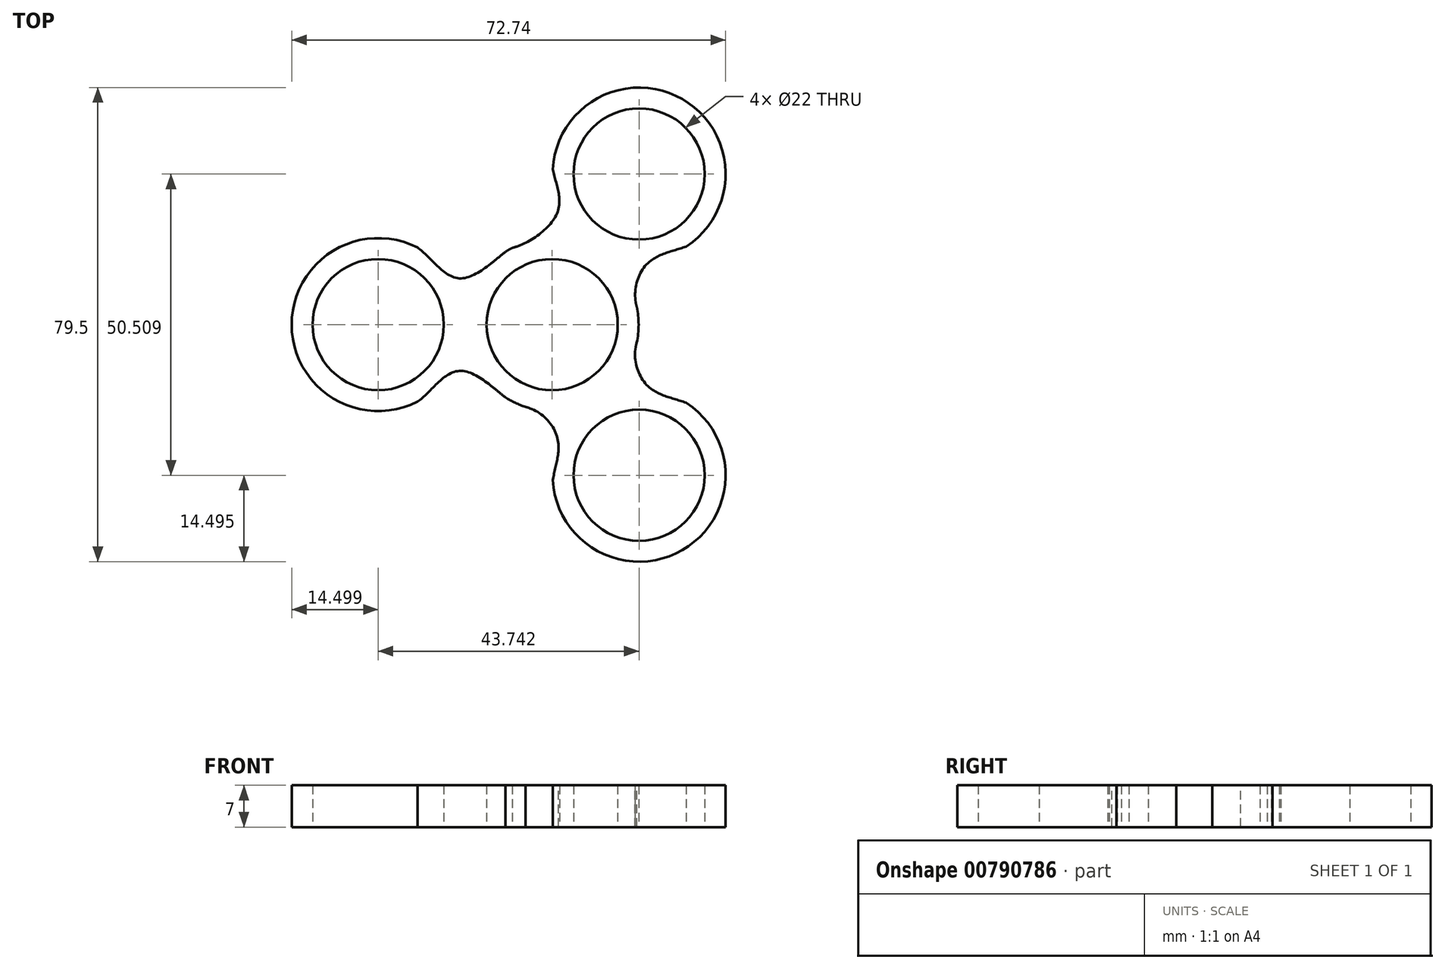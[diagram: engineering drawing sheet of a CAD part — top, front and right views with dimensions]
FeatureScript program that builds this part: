
annotation { "Feature Type Name" : "Feature", "Feature Type Description" : "" }
export const myFeature = defineFeature(function(context is Context, id is Id, definition is map)
    precondition{}
    {
        {
            var Q0;
            Q0=qCreatedBy(makeId("Top.planeOp"),FACE);
            var sketch = newSketch(context, id + "F0", { "sketchPlane" : qUnion([Q0])});
            skCircle(sketch, "E0", {"center": v(0, 0) * mm, "radius": 14.5 * mm});
            skCircle(sketch, "E1", {"center": v(-29.16, 0) * mm, "radius": 14.5 * mm});
            skCircle(sketch, "E2", {"center": v(14.58, 25.25) * mm, "radius": 14.5 * mm});
            skCircle(sketch, "E3", {"center": v(14.58, -25.25) * mm, "radius": 14.5 * mm});
            skLineSegment(sketch, "E4", {"start": v(14.58, 25.25) * mm, "end": v(-29.16, 0) * mm, "construction": true});
            skLineSegment(sketch, "E5", {"start": v(14.58, -25.25) * mm, "end": v(-29.16, 0) * mm, "construction": true});
            skLineSegment(sketch, "E6", {"start": v(14.58, -25.25) * mm, "end": v(14.58, 25.25) * mm, "construction": true});
            skLineSegment(sketch, "E7", {"start": v(14.58, 25.25) * mm, "end": v(0, 0) * mm, "construction": true});
            skLineSegment(sketch, "E8", {"start": v(-29.16, 0) * mm, "end": v(0, 0) * mm, "construction": true});
            skLineSegment(sketch, "E9", {"start": v(14.58, -25.25) * mm, "end": v(0, 0) * mm, "construction": true});
            skPoint(sketch, "E10.0.internal.snap0", {"position": v(-7.3, 12.63) * mm});
            skFitSpline(sketch, "E11", {"points": [v(-22.59, 12.92) * mm, v(-15.7, 7.77) * mm, v(-7.81, 12.22) * mm], "startDerivative": vector(12.46, -7.7) * mm, "endDerivative": vector(11.22, 8.55) * mm});
            skLineSegment(sketch, "E12", {"start": v(-29.16, 0) * mm, "end": v(-22.59, 12.92) * mm, "construction": true});
            skPoint(sketch, "E13", {"position": v(-22.59, -12.92) * mm});
            skLineSegment(sketch, "E14", {"start": v(-22.59, -12.92) * mm, "end": v(0, 0) * mm, "construction": true});
            skLineSegment(sketch, "E15", {"start": v(-22.59, 12.92) * mm, "end": v(0, 0) * mm, "construction": true});
            skPoint(sketch, "E16", {"position": v(-20.54, -11.66) * mm});
            skLineSegment(sketch, "E17", {"start": v(-20.54, -11.66) * mm, "end": v(0, 0) * mm, "construction": true});
            skLineSegment(sketch, "E18", {"start": v(-20.54, 11.66) * mm, "end": v(0, 0) * mm, "construction": true});
            skPoint(sketch, "E19", {"position": v(-9.7, -10.77) * mm});
            skLineSegment(sketch, "E20", {"start": v(-9.7, 10.77) * mm, "end": v(-29.16, 0) * mm, "construction": true});
            skLineSegment(sketch, "E21", {"start": v(-9.7, -10.77) * mm, "end": v(-29.16, 0) * mm, "construction": true});
            skPoint(sketch, "E22", {"position": v(-7.81, -12.22) * mm});
            skLineSegment(sketch, "E23", {"start": v(-7.81, -12.22) * mm, "end": v(-29.16, 0) * mm, "construction": true});
            skLineSegment(sketch, "E24", {"start": v(-7.81, 12.22) * mm, "end": v(-29.16, 0) * mm, "construction": true});
            skFitSpline(sketch, "E25.MirrorCS", {"points": [v(-22.59, -12.92) * mm, v(-15.7, -7.77) * mm, v(-7.81, -12.22) * mm], "startDerivative": vector(12.46, 7.7) * mm, "endDerivative": vector(11.22, -8.55) * mm});
            skPoint(sketch, "E26", {"position": v(22.49, 13.1) * mm});
            skLineSegment(sketch, "E27", {"start": v(22.49, 13.1) * mm, "end": v(0, 0) * mm, "construction": true});
            skLineSegment(sketch, "E28", {"start": v(14.49, 0.66) * mm, "end": v(14.58, 25.25) * mm, "construction": true});
            skFitSpline(sketch, "E29", {"points": [v(22.49, 13.1) * mm, v(15.9, 10.17) * mm, v(14.19, 2.99) * mm], "startDerivative": vector(-14.26, -4.9) * mm, "endDerivative": vector(4.41, -14.5) * mm});
            skPoint(sketch, "E30", {"position": v(0.1, 26.02) * mm});
            skLineSegment(sketch, "E31", {"start": v(0.1, 26.02) * mm, "end": v(0, 0) * mm, "construction": true});
            skPoint(sketch, "E32", {"position": v(-6.67, 12.87) * mm});
            skLineSegment(sketch, "E33", {"start": v(-6.67, 12.87) * mm, "end": v(14.58, 25.25) * mm, "construction": true});
            skFitSpline(sketch, "E34.MirrorCS", {"points": [v(0.1, 26.02) * mm, v(0.9, 18.84) * mm, v(-6.67, 12.87) * mm], "startDerivative": vector(2.98, -14.78) * mm, "endDerivative": vector(-14.74, -3.52) * mm});
            skPoint(sketch, "E35", {"position": v(14.49, -0.66) * mm});
            skPoint(sketch, "E36", {"position": v(22.49, -13.1) * mm});
            skPoint(sketch, "E37", {"position": v(0.1, -26.02) * mm});
            skPoint(sketch, "E38", {"position": v(-6.67, -12.87) * mm});
            skLineSegment(sketch, "E39", {"start": v(0.1, -26.02) * mm, "end": v(0, 0) * mm, "construction": true});
            skLineSegment(sketch, "E40", {"start": v(22.49, -13.1) * mm, "end": v(0, 0) * mm, "construction": true});
            skLineSegment(sketch, "E41", {"start": v(-6.67, -12.87) * mm, "end": v(14.58, -25.25) * mm, "construction": true});
            skLineSegment(sketch, "E42", {"start": v(14.49, -0.66) * mm, "end": v(14.58, -25.25) * mm, "construction": true});
            skFitSpline(sketch, "E43.MirrorCS", {"points": [v(22.49, -13.1) * mm, v(15.92, -10.18) * mm, v(14.18, -3.05) * mm], "startDerivative": vector(-14.3, 4.84) * mm, "endDerivative": vector(4.49, 14.52) * mm});
            skFitSpline(sketch, "E44", {"points": [v(0.1, -26.02) * mm, v(0.85, -18.88) * mm, v(-4.45, -13.8) * mm], "startDerivative": vector(2.96, 14.81) * mm, "endDerivative": vector(-14.82, 3.37) * mm});
            skCircle(sketch, "E45", {"center": v(-29.16, 0) * mm, "radius": 11 * mm});
            skCircle(sketch, "E46", {"center": v(14.58, 25.25) * mm, "radius": 11 * mm});
            skCircle(sketch, "E47", {"center": v(14.58, -25.25) * mm, "radius": 11 * mm});
            skCircle(sketch, "E48", {"center": v(0, 0) * mm, "radius": 11 * mm});
            skSolve(sketch);
        }
        {
            var Q0;
            {var subQ0=sQuery(id+"F0.wireOp",EDGE,"E11");var subQ1=sQuery(id+"F0.wireOp",EDGE,"E1");var subQ2=makeQuery(id+"F0.imprint","INTERSECT",VERTEX,{"disambiguationData":[OD(0.0)],"derivedFrom":[subQ1,subQ0]});Q0=makeQuery(id+"F0.imprint","IMPRINT",FACE,{"disambiguationData":[TD([[makeQuery(id+"F0.imprint","IMPRINT",EDGE,{"disambiguationData":[TD([[subQ2,-1.0]])],"derivedFrom":subQ1}),1.0]])]});}
            var Q1;
            {var subQ0=sQuery(id+"F0.wireOp",EDGE,"E11");var subQ1=sQuery(id+"F0.wireOp",EDGE,"E0");var subQ2=makeQuery(id+"F0.imprint","INTERSECT",VERTEX,{"disambiguationData":[OD(1.0)],"derivedFrom":[subQ1,subQ0]});Q1=makeQuery(id+"F0.imprint","IMPRINT",FACE,{"disambiguationData":[TD([[makeQuery(id+"F0.imprint","IMPRINT",EDGE,{"disambiguationData":[TD([[subQ2,-1.0]])],"derivedFrom":subQ1}),-1.0]])]});}
            var Q2;
            {var subQ1=sQuery(id+"F0.wireOp",EDGE,"E0");var subQ4=sQuery(id+"F0.wireOp",EDGE,"E29");var subQ6=makeQuery(id+"F0.imprint","INTERSECT",VERTEX,{"disambiguationData":[OD(1.0)],"derivedFrom":[subQ1,subQ4]});Q2=makeQuery(id+"F0.imprint","IMPRINT",FACE,{"disambiguationData":[TD([[makeQuery(id+"F0.imprint","IMPRINT",EDGE,{"disambiguationData":[TD([[subQ6,-1.0]])],"derivedFrom":subQ1}),1.0]])]});}
            var Q3;
            {var subQ0=sQuery(id+"F0.wireOp",EDGE,"E29");var subQ1=sQuery(id+"F0.wireOp",EDGE,"E0");var subQ2=makeQuery(id+"F0.imprint","INTERSECT",VERTEX,{"disambiguationData":[OD(1.0)],"derivedFrom":[subQ1,subQ0]});Q3=makeQuery(id+"F0.imprint","IMPRINT",FACE,{"disambiguationData":[TD([[makeQuery(id+"F0.imprint","IMPRINT",EDGE,{"disambiguationData":[TD([[subQ2,-1.0]])],"derivedFrom":subQ1}),-1.0]])]});}
            var Q4;
            {var subQ0=sQuery(id+"F0.wireOp",EDGE,"E34.MirrorCS");var subQ1=sQuery(id+"F0.wireOp",EDGE,"E2");var subQ2=makeQuery(id+"F0.imprint","INTERSECT",VERTEX,{"disambiguationData":[OD(1.0)],"derivedFrom":[subQ1,subQ0]});Q4=makeQuery(id+"F0.imprint","IMPRINT",FACE,{"disambiguationData":[TD([[makeQuery(id+"F0.imprint","IMPRINT",EDGE,{"disambiguationData":[TD([[subQ2,-1.0]])],"derivedFrom":subQ1}),1.0]])]});}
            var Q5;
            {var subQ0=sQuery(id+"F0.wireOp",EDGE,"E43.MirrorCS");var subQ1=sQuery(id+"F0.wireOp",EDGE,"E3");var subQ2=makeQuery(id+"F0.imprint","INTERSECT",VERTEX,{"disambiguationData":[OD(1.0)],"derivedFrom":[subQ1,subQ0]});Q5=makeQuery(id+"F0.imprint","IMPRINT",FACE,{"disambiguationData":[TD([[makeQuery(id+"F0.imprint","IMPRINT",EDGE,{"disambiguationData":[TD([[subQ2,-1.0]])],"derivedFrom":subQ1}),1.0]])]});}
            var Q6;
            {var subQ0=sQuery(id+"F0.wireOp",EDGE,"E44");var subQ1=sQuery(id+"F0.wireOp",EDGE,"E0");var subQ2=makeQuery(id+"F0.imprint","INTERSECT",VERTEX,{"disambiguationData":[OD(1.0)],"derivedFrom":[subQ1,subQ0]});Q6=makeQuery(id+"F0.imprint","IMPRINT",FACE,{"disambiguationData":[TD([[makeQuery(id+"F0.imprint","IMPRINT",EDGE,{"disambiguationData":[TD([[subQ2,-1.0]])],"derivedFrom":subQ1}),-1.0]])]});}
            extrude(context, id + "F1", {"entities" : qUnion([Q0, Q1, Q2, Q3, Q4, Q5, Q6]), "depth" : 7 * mm, "offsetDistance" : 25 * mm});
        }
    });
